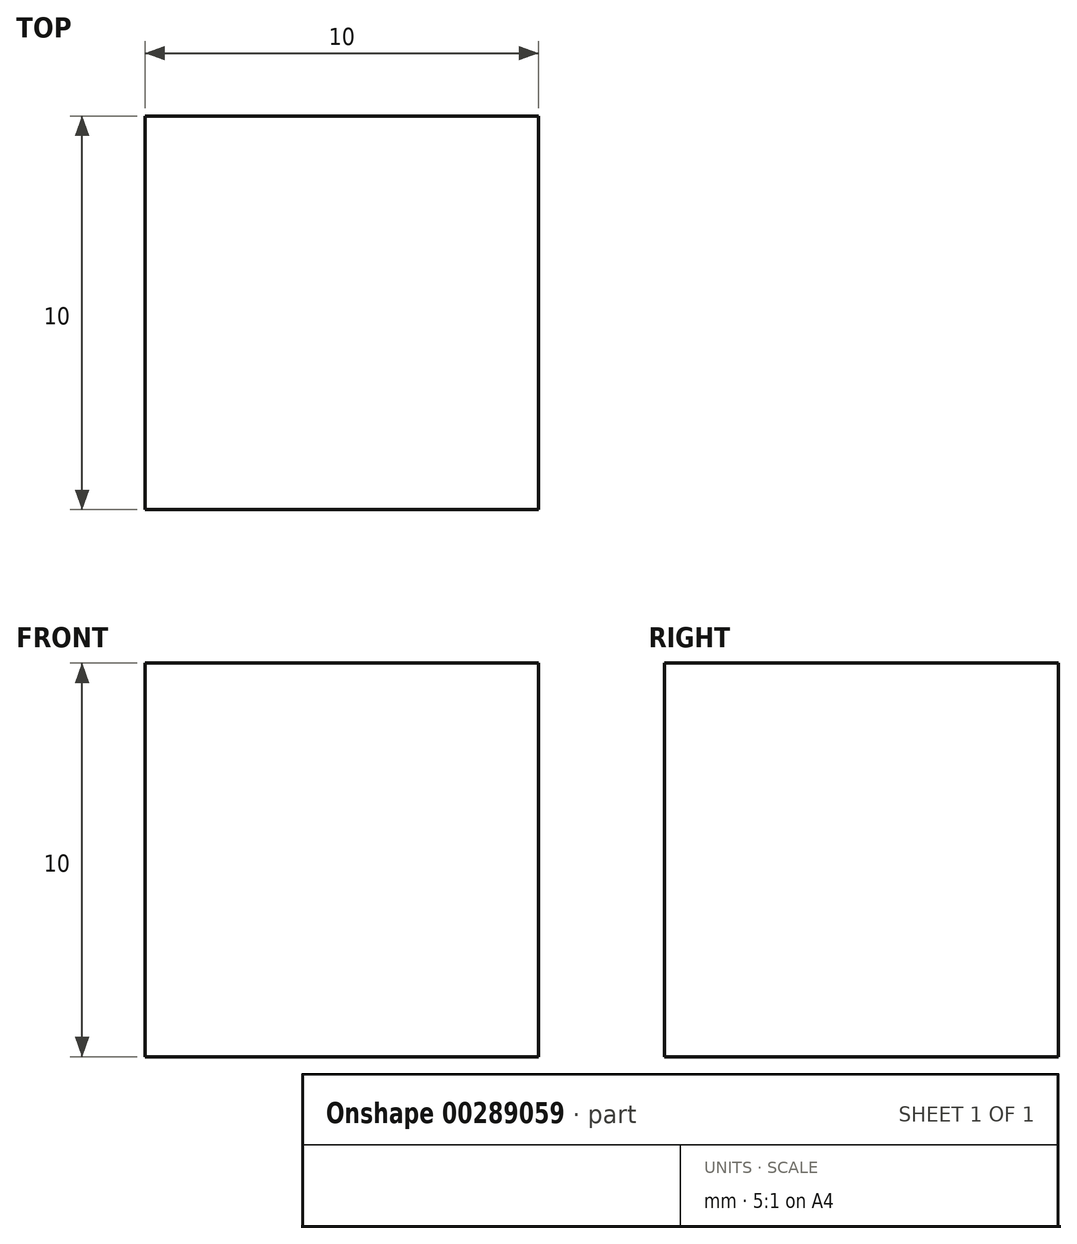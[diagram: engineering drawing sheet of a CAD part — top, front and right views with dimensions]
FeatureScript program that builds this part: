
annotation { "Feature Type Name" : "Feature", "Feature Type Description" : "" }
export const myFeature = defineFeature(function(context is Context, id is Id, definition is map)
    precondition{}
    {
        {
            var Q0;
            Q0=qCreatedBy(makeId("Top.planeOp"),FACE);
            var sketch = newSketch(context, id + "F0", { "sketchPlane" : qUnion([Q0])});
            skLineSegment(sketch, "E0.bottom", {"start": v(5, -5) * mm, "end": v(-5, -5) * mm});
            skLineSegment(sketch, "E0.top", {"start": v(5, 5) * mm, "end": v(-5, 5) * mm});
            skLineSegment(sketch, "E0.left", {"start": v(5, -5) * mm, "end": v(5, 5) * mm});
            skLineSegment(sketch, "E0.right", {"start": v(-5, -5) * mm, "end": v(-5, 5) * mm});
            skPoint(sketch, "E0.middle", {"position": v(0, 0) * mm});
            skSolve(sketch);
        }
        {
            var Q0;
            Q0 = qSketchRegion(id + "F0", true);
            extrude(context, id + "F1", {"entities" : qUnion([Q0]), "endBound" : BoundingType.SYMMETRIC, "depth" : 10 * mm});
        }
    });
